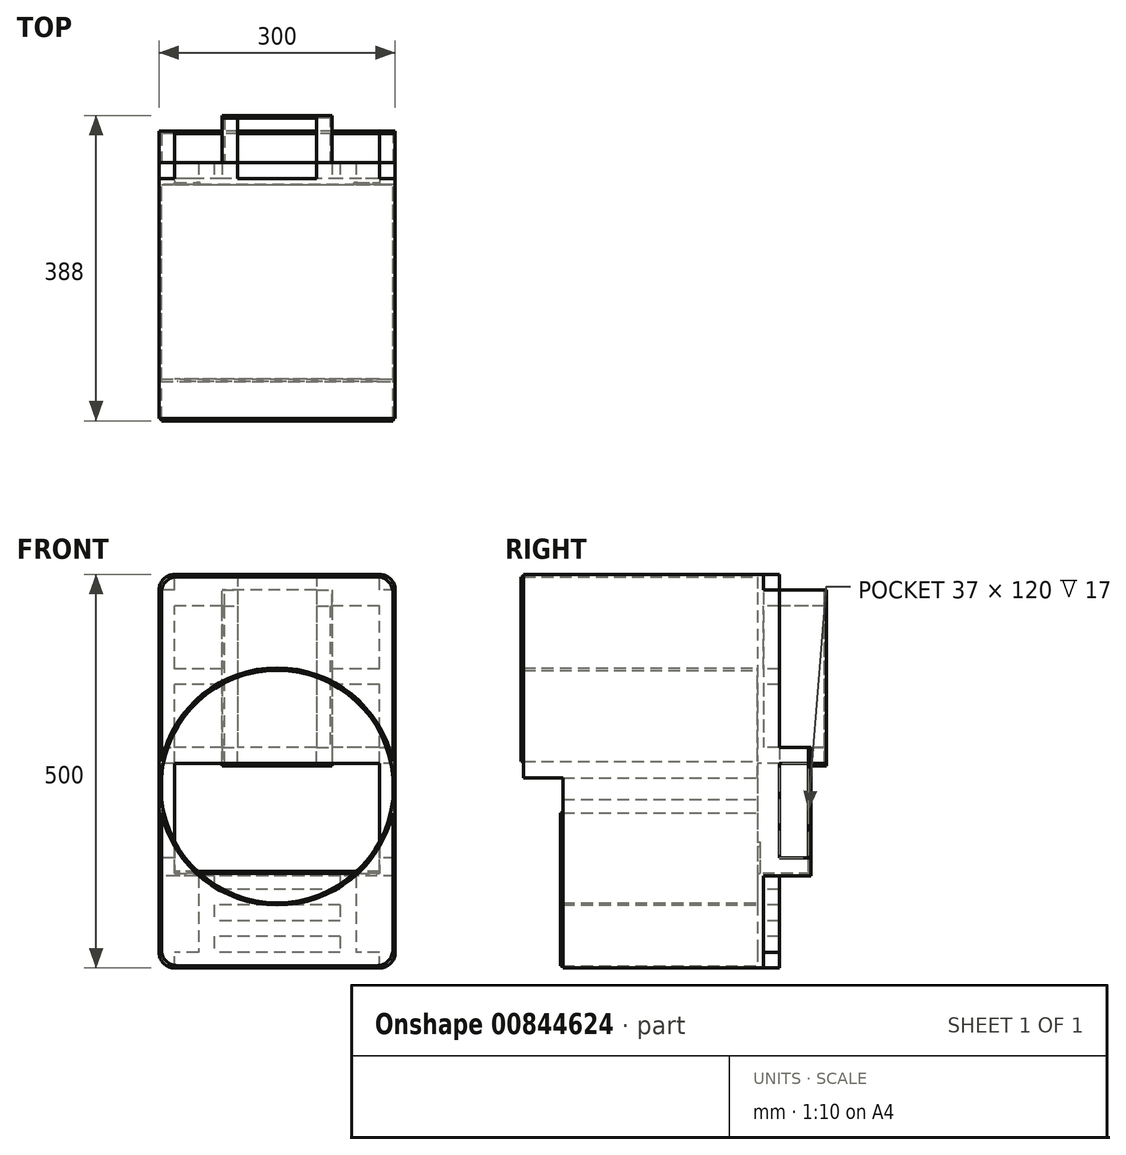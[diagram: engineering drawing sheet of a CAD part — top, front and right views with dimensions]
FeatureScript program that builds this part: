
annotation { "Feature Type Name" : "Feature", "Feature Type Description" : "" }
export const myFeature = defineFeature(function(context is Context, id is Id, definition is map)
    precondition{}
    {
        {
            var Q0;
            Q0=qCreatedBy(makeId("Front.planeOp"),FACE);
            var sketch = newSketch(context, id + "F0", { "sketchPlane" : qUnion([Q0])});
            skLineSegment(sketch, "E0.bottom", {"start": v(130, -250) * mm, "end": v(-130, -250) * mm});
            skLineSegment(sketch, "E0.top", {"start": v(130, 250) * mm, "end": v(-130, 250) * mm});
            skLineSegment(sketch, "E0.left", {"start": v(150, -230) * mm, "end": v(150, 230) * mm});
            skLineSegment(sketch, "E0.right", {"start": v(-150, -230) * mm, "end": v(-150, 230) * mm});
            skPoint(sketch, "E0.middle", {"position": v(0, 0) * mm});
            skPoint(sketch, "E1.visualSharp", {"position": v(-150, 250) * mm});
            skArc(sketch, "E1.filletArc", {"start": v(-130, 250) * mm, "mid": v(-144.14, 244.14) * mm, "end": v(-150, 230) * mm});
            skPoint(sketch, "E2.visualSharp", {"position": v(150, 250) * mm});
            skArc(sketch, "E2.filletArc", {"start": v(150, 230) * mm, "mid": v(144.14, 244.14) * mm, "end": v(130, 250) * mm});
            skPoint(sketch, "E3.visualSharp", {"position": v(-150, -250) * mm});
            skArc(sketch, "E3.filletArc", {"start": v(-150, -230) * mm, "mid": v(-144.14, -244.14) * mm, "end": v(-130, -250) * mm});
            skPoint(sketch, "E4.visualSharp", {"position": v(150, -250) * mm});
            skArc(sketch, "E4.filletArc", {"start": v(130, -250) * mm, "mid": v(144.14, -244.14) * mm, "end": v(150, -230) * mm});
            skSolve(sketch);
        }
        {
            var Q0;
            Q0=makeQuery(id+"F0.imprint","IMPRINT",FACE,{"disambiguationData":[TD([[makeQuery(id+"F0.imprint","IMPRINT",EDGE,{"derivedFrom":sQuery(id+"F0.wireOp",EDGE,"E0.bottom")}),-1.0]])]});
            extrude(context, id + "F1", {"entities" : qUnion([Q0]), "depth" : 5 * mm, "offsetDistance" : 25 * mm});
        }
        {
            var Q0;
            Q0=makeQuery(id+"F1.opExtrude","CAP_FACE",FACE,{"disambiguationData":[OSD([sQuery(id+"F0.wireOp",EDGE,"E0.bottom"),sQuery(id+"F0.wireOp",EDGE,"E0.top"),sQuery(id+"F0.wireOp",EDGE,"E0.left"),sQuery(id+"F0.wireOp",EDGE,"E0.right"),sQuery(id+"F0.wireOp",EDGE,"E1.filletArc"),sQuery(id+"F0.wireOp",EDGE,"E2.filletArc"),sQuery(id+"F0.wireOp",EDGE,"E3.filletArc"),sQuery(id+"F0.wireOp",EDGE,"E4.filletArc")])],"isStart":true});
            var sketch = newSketch(context, id + "F2", { "sketchPlane" : qUnion([Q0])});
            skLineSegment(sketch, "E5.0", {"start": v(-150, 230) * mm, "end": v(-50, 230) * mm});
            skLineSegment(sketch, "E6", {"start": v(-100, -130) * mm, "end": v(-100, -230) * mm});
            skLineSegment(sketch, "E7", {"start": v(100, -130) * mm, "end": v(100, -230) * mm});
            skLineSegment(sketch, "E8.trimOffspring", {"start": v(-130, -130) * mm, "end": v(-130, 250) * mm});
            skLineSegment(sketch, "E9.trimOffspring", {"start": v(130, -130) * mm, "end": v(130, 250) * mm});
            skLineSegment(sketch, "E10.bottom", {"start": v(-130, -250) * mm, "end": v(130, -250) * mm});
            skLineSegment(sketch, "E10.top", {"start": v(-130, -230) * mm, "end": v(130, -230) * mm});
            skLineSegment(sketch, "E10.left", {"start": v(-130, -250) * mm, "end": v(-130, -230) * mm});
            skLineSegment(sketch, "E10.right", {"start": v(130, -250) * mm, "end": v(130, -230) * mm});
            skLineSegment(sketch, "E11.0", {"start": v(-80, -210) * mm, "end": v(80, -210) * mm});
            skLineSegment(sketch, "E12.0", {"start": v(-80, -150) * mm, "end": v(80, -150) * mm});
            skLineSegment(sketch, "E13.0", {"start": v(-150, -130) * mm, "end": v(150, -130) * mm});
            skLineSegment(sketch, "E14.0", {"start": v(-150, -110) * mm, "end": v(150, -110) * mm});
            skLineSegment(sketch, "E15.0", {"start": v(-80, -130) * mm, "end": v(-80, -230) * mm});
            skLineSegment(sketch, "E16.0", {"start": v(80, -130) * mm, "end": v(80, -230) * mm});
            skLineSegment(sketch, "E17.trimOffspring", {"start": v(-80, -190) * mm, "end": v(80, -190) * mm});
            skLineSegment(sketch, "E18.trimOffspring", {"start": v(-80, -170) * mm, "end": v(80, -170) * mm});
            skLineSegment(sketch, "E19.0", {"start": v(-130, 130) * mm, "end": v(-70, 130) * mm});
            skLineSegment(sketch, "E20.0", {"start": v(-130, 110) * mm, "end": v(-70, 110) * mm});
            skLineSegment(sketch, "E21", {"start": v(-150, 30) * mm, "end": v(150, 30) * mm});
            skLineSegment(sketch, "E22.0", {"start": v(-150, 10) * mm, "end": v(150, 10) * mm});
            skLineSegment(sketch, "E23", {"start": v(-70, 230) * mm, "end": v(-70, 10) * mm});
            skLineSegment(sketch, "E24", {"start": v(70, 230) * mm, "end": v(70, 10) * mm});
            skLineSegment(sketch, "E25.0", {"start": v(50, 250) * mm, "end": v(50, 10) * mm});
            skLineSegment(sketch, "E26.0", {"start": v(-50, 250) * mm, "end": v(-50, 10) * mm});
            skLineSegment(sketch, "E27.trimOffspring", {"start": v(50, 230) * mm, "end": v(150, 230) * mm});
            skLineSegment(sketch, "E28.trimOffspring", {"start": v(70, 130) * mm, "end": v(130, 130) * mm});
            skLineSegment(sketch, "E29.trimOffspring", {"start": v(70, 110) * mm, "end": v(130, 110) * mm});
            skLineSegment(sketch, "E30.0", {"start": v(-130, 210) * mm, "end": v(-50, 210) * mm});
            skLineSegment(sketch, "E31.0", {"start": v(50, 210) * mm, "end": v(130, 210) * mm});
            skPoint(sketch, "E32.orphan", {"position": v(130, 30) * mm});
            skSolve(sketch);
        }
        {
            var Q0;
            Q0=makeQuery(id+"F2.imprint","IMPRINT",FACE,{"disambiguationData":[TD([[makeQuery(id+"F2.imprint","IMPRINT",EDGE,{"derivedFrom":sQuery(id+"F2.wireOp",EDGE,"E10.bottom")}),1.0]])]});
            var Q1;
            {var subQ0=sQuery(id+"F2.wireOp",EDGE,"E11.0");Q1=makeQuery(id+"F2.imprint","IMPRINT",FACE,{"disambiguationData":[TD([[makeQuery(id+"F2.imprint","IMPRINT",EDGE,{"derivedFrom":subQ0}),1.0]])]});}
            var Q2;
            {var subQ0=sQuery(id+"F2.wireOp",EDGE,"E12.0");Q2=makeQuery(id+"F2.imprint","IMPRINT",FACE,{"disambiguationData":[TD([[makeQuery(id+"F2.imprint","IMPRINT",EDGE,{"derivedFrom":subQ0}),-1.0]])]});}
            var Q3;
            {var subQ0=sQuery(id+"F2.wireOp",EDGE,"E13.0");var subQ2=sQuery(id+"F2.wireOp",EDGE,"E8.trimOffspring");var subQ3=makeQuery(id+"F2.imprint","INTERSECT",VERTEX,{"derivedFrom":[subQ2,subQ0]});Q3=makeQuery(id+"F2.imprint","IMPRINT",FACE,{"disambiguationData":[TD([[makeQuery(id+"F2.imprint","IMPRINT",EDGE,{"disambiguationData":[TD([[subQ3,-1.0]])],"derivedFrom":subQ2}),-1.0]])]});}
            var Q4;
            {var subQ4=sQuery(id+"F2.wireOp",EDGE,"E6");Q4=makeQuery(id+"F2.imprint","IMPRINT",FACE,{"disambiguationData":[TD([[makeQuery(id+"F2.imprint","IMPRINT",EDGE,{"derivedFrom":subQ4}),1.0]])]});}
            var Q5;
            {var subQ4=sQuery(id+"F2.wireOp",EDGE,"E7");Q5=makeQuery(id+"F2.imprint","IMPRINT",FACE,{"disambiguationData":[TD([[makeQuery(id+"F2.imprint","IMPRINT",EDGE,{"derivedFrom":subQ4}),-1.0]])]});}
            var Q6;
            {var subQ0=sQuery(id+"F2.wireOp",EDGE,"E13.0");var subQ1=sQuery(id+"F2.wireOp",EDGE,"E8.trimOffspring");var subQ2=makeQuery(id+"F2.imprint","INTERSECT",VERTEX,{"derivedFrom":[subQ1,subQ0]});Q6=makeQuery(id+"F2.imprint","IMPRINT",FACE,{"disambiguationData":[TD([[makeQuery(id+"F2.imprint","IMPRINT",EDGE,{"disambiguationData":[TD([[subQ2,-1.0]])],"derivedFrom":subQ1}),1.0]])]});}
            var Q7;
            {var subQ0=sQuery(id+"F2.wireOp",EDGE,"E14.0");var subQ1=sQuery(id+"F2.wireOp",EDGE,"E8.trimOffspring");var subQ2=makeQuery(id+"F2.imprint","INTERSECT",VERTEX,{"derivedFrom":[subQ1,subQ0]});Q7=makeQuery(id+"F2.imprint","IMPRINT",FACE,{"disambiguationData":[TD([[makeQuery(id+"F2.imprint","IMPRINT",EDGE,{"disambiguationData":[TD([[subQ2,-1.0]])],"derivedFrom":subQ1}),1.0]])]});}
            var Q8;
            {var subQ0=sQuery(id+"F2.wireOp",EDGE,"E22.0");var subQ1=sQuery(id+"F2.wireOp",EDGE,"E8.trimOffspring");var subQ2=makeQuery(id+"F2.imprint","INTERSECT",VERTEX,{"derivedFrom":[subQ1,subQ0]});Q8=makeQuery(id+"F2.imprint","IMPRINT",FACE,{"disambiguationData":[TD([[makeQuery(id+"F2.imprint","IMPRINT",EDGE,{"disambiguationData":[TD([[subQ2,-1.0]])],"derivedFrom":subQ1}),1.0]])]});}
            var Q9;
            {var subQ0=sQuery(id+"F2.wireOp",EDGE,"E22.0");var subQ1=sQuery(id+"F2.wireOp",EDGE,"E8.trimOffspring");var subQ2=makeQuery(id+"F2.imprint","INTERSECT",VERTEX,{"derivedFrom":[subQ1,subQ0]});Q9=makeQuery(id+"F2.imprint","IMPRINT",FACE,{"disambiguationData":[TD([[makeQuery(id+"F2.imprint","IMPRINT",EDGE,{"disambiguationData":[TD([[subQ2,-1.0]])],"derivedFrom":subQ1}),-1.0]])]});}
            var Q10;
            {var subQ0=sQuery(id+"F2.wireOp",EDGE,"E23");var subQ1=sQuery(id+"F2.wireOp",EDGE,"E21");var subQ2=makeQuery(id+"F2.imprint","INTERSECT",VERTEX,{"derivedFrom":[subQ1,subQ0]});Q10=makeQuery(id+"F2.imprint","IMPRINT",FACE,{"disambiguationData":[TD([[makeQuery(id+"F2.imprint","IMPRINT",EDGE,{"disambiguationData":[TD([[subQ2,-1.0]])],"derivedFrom":subQ1}),-1.0]])]});}
            var Q11;
            {var subQ0=sQuery(id+"F2.wireOp",EDGE,"E26.0");var subQ1=sQuery(id+"F2.wireOp",EDGE,"E21");var subQ2=makeQuery(id+"F2.imprint","INTERSECT",VERTEX,{"derivedFrom":[subQ1,subQ0]});Q11=makeQuery(id+"F2.imprint","IMPRINT",FACE,{"disambiguationData":[TD([[makeQuery(id+"F2.imprint","IMPRINT",EDGE,{"disambiguationData":[TD([[subQ2,-1.0]])],"derivedFrom":subQ1}),-1.0]])]});}
            var Q12;
            {var subQ0=sQuery(id+"F2.wireOp",EDGE,"E25.0");var subQ1=sQuery(id+"F2.wireOp",EDGE,"E21");var subQ2=makeQuery(id+"F2.imprint","INTERSECT",VERTEX,{"derivedFrom":[subQ1,subQ0]});Q12=makeQuery(id+"F2.imprint","IMPRINT",FACE,{"disambiguationData":[TD([[makeQuery(id+"F2.imprint","IMPRINT",EDGE,{"disambiguationData":[TD([[subQ2,-1.0]])],"derivedFrom":subQ1}),-1.0]])]});}
            var Q13;
            {var subQ0=sQuery(id+"F2.wireOp",EDGE,"E22.0");var subQ1=sQuery(id+"F2.wireOp",EDGE,"E9.trimOffspring");var subQ2=makeQuery(id+"F2.imprint","INTERSECT",VERTEX,{"derivedFrom":[subQ1,subQ0]});Q13=makeQuery(id+"F2.imprint","IMPRINT",FACE,{"disambiguationData":[TD([[makeQuery(id+"F2.imprint","IMPRINT",EDGE,{"disambiguationData":[TD([[subQ2,-1.0]])],"derivedFrom":subQ1}),1.0]])]});}
            var Q14;
            {var subQ0=sQuery(id+"F2.wireOp",EDGE,"E22.0");var subQ1=sQuery(id+"F2.wireOp",EDGE,"E9.trimOffspring");var subQ2=makeQuery(id+"F2.imprint","INTERSECT",VERTEX,{"derivedFrom":[subQ1,subQ0]});Q14=makeQuery(id+"F2.imprint","IMPRINT",FACE,{"disambiguationData":[TD([[makeQuery(id+"F2.imprint","IMPRINT",EDGE,{"disambiguationData":[TD([[subQ2,-1.0]])],"derivedFrom":subQ1}),-1.0]])]});}
            var Q15;
            {var subQ0=sQuery(id+"F2.wireOp",EDGE,"E14.0");var subQ1=sQuery(id+"F2.wireOp",EDGE,"E9.trimOffspring");var subQ2=makeQuery(id+"F2.imprint","INTERSECT",VERTEX,{"derivedFrom":[subQ1,subQ0]});Q15=makeQuery(id+"F2.imprint","IMPRINT",FACE,{"disambiguationData":[TD([[makeQuery(id+"F2.imprint","IMPRINT",EDGE,{"disambiguationData":[TD([[subQ2,-1.0]])],"derivedFrom":subQ1}),-1.0]])]});}
            var Q16;
            {var subQ0=sQuery(id+"F2.wireOp",EDGE,"E13.0");var subQ1=sQuery(id+"F2.wireOp",EDGE,"E9.trimOffspring");var subQ2=makeQuery(id+"F2.imprint","INTERSECT",VERTEX,{"derivedFrom":[subQ1,subQ0]});Q16=makeQuery(id+"F2.imprint","IMPRINT",FACE,{"disambiguationData":[TD([[makeQuery(id+"F2.imprint","IMPRINT",EDGE,{"disambiguationData":[TD([[subQ2,-1.0]])],"derivedFrom":subQ1}),-1.0]])]});}
            var Q17;
            {var subQ2=sQuery(id+"F2.wireOp",EDGE,"E21");var subQ7=sQuery(id+"F2.wireOp",EDGE,"E25.0");var subQ8=makeQuery(id+"F2.imprint","INTERSECT",VERTEX,{"derivedFrom":[subQ2,subQ7]});Q17=makeQuery(id+"F2.imprint","IMPRINT",FACE,{"disambiguationData":[TD([[makeQuery(id+"F2.imprint","IMPRINT",EDGE,{"disambiguationData":[TD([[subQ8,-1.0]])],"derivedFrom":subQ2}),1.0]])]});}
            var Q18;
            {var subQ0=sQuery(id+"F2.wireOp",EDGE,"E28.trimOffspring");Q18=makeQuery(id+"F2.imprint","IMPRINT",FACE,{"disambiguationData":[TD([[makeQuery(id+"F2.imprint","IMPRINT",EDGE,{"derivedFrom":subQ0}),-1.0]])]});}
            var Q19;
            {var subQ0=sQuery(id+"F2.wireOp",EDGE,"E9.trimOffspring");var subQ5=makeQuery(id+"F2.imprint","INTERSECT",VERTEX,{"derivedFrom":[subQ0,sQuery(id+"F2.wireOp",EDGE,"E29.trimOffspring")]});Q19=makeQuery(id+"F2.imprint","IMPRINT",FACE,{"disambiguationData":[TD([[makeQuery(id+"F2.imprint","IMPRINT",EDGE,{"disambiguationData":[TD([[subQ5,1.0]])],"derivedFrom":subQ0}),-1.0]])]});}
            var Q20;
            {var subQ0=sQuery(id+"F2.wireOp",EDGE,"E31.0");var subQ1=sQuery(id+"F2.wireOp",EDGE,"E9.trimOffspring");var subQ2=makeQuery(id+"F2.imprint","INTERSECT",VERTEX,{"derivedFrom":[subQ1,subQ0]});Q20=makeQuery(id+"F2.imprint","IMPRINT",FACE,{"disambiguationData":[TD([[makeQuery(id+"F2.imprint","IMPRINT",EDGE,{"disambiguationData":[TD([[subQ2,-1.0]])],"derivedFrom":subQ1}),1.0]])]});}
            var Q21;
            {var subQ0=sQuery(id+"F2.wireOp",EDGE,"E27.trimOffspring");var subQ1=sQuery(id+"F2.wireOp",EDGE,"E24");var subQ2=makeQuery(id+"F2.imprint","INTERSECT",VERTEX,{"derivedFrom":[subQ1,subQ0]});Q21=makeQuery(id+"F2.imprint","IMPRINT",FACE,{"disambiguationData":[TD([[makeQuery(id+"F2.imprint","IMPRINT",EDGE,{"disambiguationData":[TD([[subQ2,-1.0]])],"derivedFrom":subQ1}),-1.0]])]});}
            var Q22;
            {var subQ4=sQuery(id+"F2.wireOp",EDGE,"E25.0");var subQ6=makeQuery(id+"F1.opExtrude","CAP_EDGE",EDGE,{"disambiguationData":[OSD([sQuery(id+"F0.wireOp",EDGE,"E0.top")])],"isStart":true});var subQ7=makeQuery(id+"F2.imprint","INTERSECT",VERTEX,{"derivedFrom":[subQ6,subQ4]});Q22=makeQuery(id+"F2.imprint","IMPRINT",FACE,{"disambiguationData":[TD([[makeQuery(id+"F2.imprint","IMPRINT",EDGE,{"disambiguationData":[TD([[subQ7,-1.0]])],"derivedFrom":subQ4}),1.0]])]});}
            var Q23;
            {var subQ1=sQuery(id+"F2.wireOp",EDGE,"E5.0");var subQ8=makeQuery(id+"F2.imprint","INTERSECT",VERTEX,{"derivedFrom":[subQ1,sQuery(id+"F2.wireOp",EDGE,"E23")]});Q23=makeQuery(id+"F2.imprint","IMPRINT",FACE,{"disambiguationData":[TD([[makeQuery(id+"F2.imprint","IMPRINT",EDGE,{"disambiguationData":[TD([[subQ8,1.0]])],"derivedFrom":subQ1}),1.0]])]});}
            var Q24;
            {var subQ0=sQuery(id+"F2.wireOp",EDGE,"E23");var subQ1=sQuery(id+"F2.wireOp",EDGE,"E5.0");var subQ2=makeQuery(id+"F2.imprint","INTERSECT",VERTEX,{"derivedFrom":[subQ1,subQ0]});Q24=makeQuery(id+"F2.imprint","IMPRINT",FACE,{"disambiguationData":[TD([[makeQuery(id+"F2.imprint","IMPRINT",EDGE,{"disambiguationData":[TD([[subQ2,1.0]])],"derivedFrom":subQ1}),-1.0]])]});}
            var Q25;
            {var subQ0=sQuery(id+"F2.wireOp",EDGE,"E23");var subQ7=sQuery(id+"F2.wireOp",EDGE,"E21");var subQ8=makeQuery(id+"F2.imprint","INTERSECT",VERTEX,{"derivedFrom":[subQ7,subQ0]});Q25=makeQuery(id+"F2.imprint","IMPRINT",FACE,{"disambiguationData":[TD([[makeQuery(id+"F2.imprint","IMPRINT",EDGE,{"disambiguationData":[TD([[subQ8,-1.0]])],"derivedFrom":subQ7}),1.0]])]});}
            var Q26;
            {var subQ0=sQuery(id+"F2.wireOp",EDGE,"E19.0");Q26=makeQuery(id+"F2.imprint","IMPRINT",FACE,{"disambiguationData":[TD([[makeQuery(id+"F2.imprint","IMPRINT",EDGE,{"derivedFrom":subQ0}),-1.0]])]});}
            var Q27;
            {var subQ0=sQuery(id+"F2.wireOp",EDGE,"E8.trimOffspring");var subQ2=makeQuery(id+"F2.imprint","INTERSECT",VERTEX,{"derivedFrom":[subQ0,sQuery(id+"F2.wireOp",EDGE,"E20.0")]});Q27=makeQuery(id+"F2.imprint","IMPRINT",FACE,{"disambiguationData":[TD([[makeQuery(id+"F2.imprint","IMPRINT",EDGE,{"disambiguationData":[TD([[subQ2,1.0]])],"derivedFrom":subQ0}),1.0]])]});}
            var Q28;
            {var subQ0=sQuery(id+"F2.wireOp",EDGE,"E26.0");var subQ1=sQuery(id+"F2.wireOp",EDGE,"E5.0");var subQ2=makeQuery(id+"F2.imprint","INTERSECT",VERTEX,{"derivedFrom":[subQ1,subQ0]});Q28=makeQuery(id+"F2.imprint","IMPRINT",FACE,{"disambiguationData":[TD([[makeQuery(id+"F2.imprint","IMPRINT",EDGE,{"disambiguationData":[TD([[subQ2,1.0]])],"derivedFrom":subQ1}),-1.0]])]});}
            extrude(context, id + "F3", {"entities" : qUnion([Q0, Q1, Q2, Q3, Q4, Q5, Q6, Q7, Q8, Q9, Q10, Q11, Q12, Q13, Q14, Q15, Q16, Q17, Q18, Q19, Q20, Q21, Q22, Q23, Q24, Q25, Q26, Q27, Q28]), "operationType" : NewBodyOperationType.ADD, "depth" : 20 * mm, "offsetDistance" : 25 * mm});
        }
        {
            var Q0;
            {var subQ0=sQuery(id+"F2.wireOp",EDGE,"E13.0");var subQ1=sQuery(id+"F2.wireOp",EDGE,"E8.trimOffspring");var subQ2=makeQuery(id+"F2.imprint","INTERSECT",VERTEX,{"derivedFrom":[subQ1,subQ0]});Q0=makeQuery(id+"F2.imprint","IMPRINT",FACE,{"disambiguationData":[TD([[makeQuery(id+"F2.imprint","IMPRINT",EDGE,{"disambiguationData":[TD([[subQ2,-1.0]])],"derivedFrom":subQ1}),1.0]])]});}
            var Q1;
            {var subQ0=sQuery(id+"F2.wireOp",EDGE,"E22.0");var subQ1=sQuery(id+"F2.wireOp",EDGE,"E8.trimOffspring");var subQ2=makeQuery(id+"F2.imprint","INTERSECT",VERTEX,{"derivedFrom":[subQ1,subQ0]});Q1=makeQuery(id+"F2.imprint","IMPRINT",FACE,{"disambiguationData":[TD([[makeQuery(id+"F2.imprint","IMPRINT",EDGE,{"disambiguationData":[TD([[subQ2,-1.0]])],"derivedFrom":subQ1}),1.0]])]});}
            var Q2;
            {var subQ0=sQuery(id+"F2.wireOp",EDGE,"E13.0");var subQ1=sQuery(id+"F2.wireOp",EDGE,"E9.trimOffspring");var subQ2=makeQuery(id+"F2.imprint","INTERSECT",VERTEX,{"derivedFrom":[subQ1,subQ0]});Q2=makeQuery(id+"F2.imprint","IMPRINT",FACE,{"disambiguationData":[TD([[makeQuery(id+"F2.imprint","IMPRINT",EDGE,{"disambiguationData":[TD([[subQ2,-1.0]])],"derivedFrom":subQ1}),-1.0]])]});}
            var Q3;
            {var subQ0=sQuery(id+"F2.wireOp",EDGE,"E22.0");var subQ1=sQuery(id+"F2.wireOp",EDGE,"E9.trimOffspring");var subQ2=makeQuery(id+"F2.imprint","INTERSECT",VERTEX,{"derivedFrom":[subQ1,subQ0]});Q3=makeQuery(id+"F2.imprint","IMPRINT",FACE,{"disambiguationData":[TD([[makeQuery(id+"F2.imprint","IMPRINT",EDGE,{"disambiguationData":[TD([[subQ2,-1.0]])],"derivedFrom":subQ1}),-1.0]])]});}
            extrude(context, id + "F4", {"entities" : qUnion([Q0, Q1, Q2, Q3]), "operationType" : NewBodyOperationType.ADD, "depth" : 60 * mm, "offsetDistance" : 25 * mm});
        }
        {
            var Q0;
            {var subQ0=sQuery(id+"F2.wireOp",EDGE,"E25.0");var subQ1=sQuery(id+"F2.wireOp",EDGE,"E21");var subQ2=makeQuery(id+"F2.imprint","INTERSECT",VERTEX,{"derivedFrom":[subQ1,subQ0]});Q0=makeQuery(id+"F2.imprint","IMPRINT",FACE,{"disambiguationData":[TD([[makeQuery(id+"F2.imprint","IMPRINT",EDGE,{"disambiguationData":[TD([[subQ2,-1.0]])],"derivedFrom":subQ1}),-1.0]])]});}
            var Q1;
            {var subQ0=sQuery(id+"F2.wireOp",EDGE,"E26.0");var subQ1=sQuery(id+"F2.wireOp",EDGE,"E5.0");var subQ2=makeQuery(id+"F2.imprint","INTERSECT",VERTEX,{"derivedFrom":[subQ1,subQ0]});Q1=makeQuery(id+"F2.imprint","IMPRINT",FACE,{"disambiguationData":[TD([[makeQuery(id+"F2.imprint","IMPRINT",EDGE,{"disambiguationData":[TD([[subQ2,1.0]])],"derivedFrom":subQ1}),-1.0]])]});}
            var Q2;
            {var subQ0=sQuery(id+"F2.wireOp",EDGE,"E27.trimOffspring");var subQ1=sQuery(id+"F2.wireOp",EDGE,"E24");var subQ2=makeQuery(id+"F2.imprint","INTERSECT",VERTEX,{"derivedFrom":[subQ1,subQ0]});Q2=makeQuery(id+"F2.imprint","IMPRINT",FACE,{"disambiguationData":[TD([[makeQuery(id+"F2.imprint","IMPRINT",EDGE,{"disambiguationData":[TD([[subQ2,-1.0]])],"derivedFrom":subQ1}),-1.0]])]});}
            var Q3;
            {var subQ0=sQuery(id+"F2.wireOp",EDGE,"E23");var subQ1=sQuery(id+"F2.wireOp",EDGE,"E21");var subQ2=makeQuery(id+"F2.imprint","INTERSECT",VERTEX,{"derivedFrom":[subQ1,subQ0]});Q3=makeQuery(id+"F2.imprint","IMPRINT",FACE,{"disambiguationData":[TD([[makeQuery(id+"F2.imprint","IMPRINT",EDGE,{"disambiguationData":[TD([[subQ2,-1.0]])],"derivedFrom":subQ1}),-1.0]])]});}
            extrude(context, id + "F5", {"entities" : qUnion([Q0, Q1, Q2, Q3]), "operationType" : NewBodyOperationType.ADD, "depth" : 80 * mm, "offsetDistance" : 25 * mm});
        }
        {
            var Q0;
            Q0=makeQuery(id+"F4.opExtrude","CAP_FACE",FACE,{"disambiguationData":[OSD([sQuery(id+"F0.wireOp",EDGE,"E0.left"),sQuery(id+"F2.wireOp",EDGE,"E8.trimOffspring"),sQuery(id+"F2.wireOp",EDGE,"E21"),sQuery(id+"F2.wireOp",EDGE,"E22.0")])],"isStart":false});
            var sketch = newSketch(context, id + "F6", { "sketchPlane" : qUnion([Q0])});
            skLineSegment(sketch, "E33", {"start": v(-70, 30) * mm, "end": v(-150, 30) * mm});
            skLineSegment(sketch, "E34", {"start": v(-150, 30) * mm, "end": v(-150, -130) * mm});
            skLineSegment(sketch, "E35", {"start": v(-150, -130) * mm, "end": v(150, -130) * mm});
            skLineSegment(sketch, "E36", {"start": v(150, -130) * mm, "end": v(150, 30) * mm});
            skLineSegment(sketch, "E37", {"start": v(150, 30) * mm, "end": v(70, 30) * mm});
            skLineSegment(sketch, "E38", {"start": v(70, 30) * mm, "end": v(70, 10) * mm});
            skLineSegment(sketch, "E39", {"start": v(-70, 30) * mm, "end": v(-70, 10) * mm});
            skLineSegment(sketch, "E40", {"start": v(-70, 10) * mm, "end": v(70, 10) * mm});
            skSolve(sketch);
        }
        {
            var Q0;
            {var subQ0=sQuery(id+"F0.wireOp",EDGE,"E0.left");var subQ1=makeQuery(id+"F1.opExtrude","CAP_EDGE",EDGE,{"disambiguationData":[OSD([subQ0])],"isStart":true});Q0=makeQuery(id+"F4.boolean.opBoolean","MERGE",FACE,{"derivedFrom":[makeQuery(id+"F3.boolean.opBoolean","MERGE",FACE,{"derivedFrom":[makeQuery(id+"F1.opExtrude","SWEPT_FACE",FACE,{"disambiguationData":[OSD([subQ0])]}),makeQuery(id+"F3.opExtrude","SWEPT_FACE",FACE,{"disambiguationData":[OSD([subQ0])]})]}),makeQuery(id+"F4.opExtrude","SWEPT_FACE",FACE,{"disambiguationData":[OSD([subQ0]),TDD([makeQuery(id+"F2.imprint","IMPRINT",EDGE,{"disambiguationData":[TD([[makeQuery(id+"F2.imprint","INTERSECT",VERTEX,{"derivedFrom":[subQ1,sQuery(id+"F2.wireOp",EDGE,"E13.0")]}),-1.0]])],"derivedFrom":subQ1})])]}),makeQuery(id+"F4.opExtrude","SWEPT_FACE",FACE,{"disambiguationData":[OSD([subQ0]),TDD([makeQuery(id+"F2.imprint","IMPRINT",EDGE,{"disambiguationData":[TD([[makeQuery(id+"F2.imprint","INTERSECT",VERTEX,{"derivedFrom":[subQ1,sQuery(id+"F2.wireOp",EDGE,"E21")]}),1.0]])],"derivedFrom":subQ1})])]})]});}
            var sketch = newSketch(context, id + "F7", { "sketchPlane" : qUnion([Q0])});
            skLineSegment(sketch, "E41.bottom", {"start": v(60, 30) * mm, "end": v(-5, 30) * mm});
            skLineSegment(sketch, "E41.top", {"start": v(60, -130) * mm, "end": v(-5, -130) * mm});
            skLineSegment(sketch, "E41.left", {"start": v(60, 30) * mm, "end": v(60, -130) * mm});
            skLineSegment(sketch, "E41.right", {"start": v(-5, 30) * mm, "end": v(-5, -130) * mm});
            skSolve(sketch);
        }
        {
            var Q0;
            {var subQ1=sQuery(id+"F2.wireOp",EDGE,"E14.0");var subQ2=sQuery(id+"F0.wireOp",EDGE,"E0.left");var subQ3=makeQuery(id+"F4.opExtrude","SWEPT_EDGE",EDGE,{"disambiguationData":[OSD([subQ2,subQ1])]});Q0=makeQuery(id+"F7.imprint","IMPRINT",FACE,{"disambiguationData":[TD([[makeQuery(id+"F7.imprint","IMPRINT",EDGE,{"derivedFrom":subQ3}),-1.0]])]});}
            extrude(context, id + "F8", {"entities" : qUnion([Q0]), "oppositeDirection" : true, "depth" : 3 * mm, "offsetDistance" : 25 * mm});
        }
        {
            var Q0;
            {var subQ0=sQuery(id+"F2.wireOp",EDGE,"E13.0");var subQ1=makeQuery(id+"F2.imprint","INTERSECT",VERTEX,{"derivedFrom":[sQuery(id+"F2.wireOp",EDGE,"E8.trimOffspring"),subQ0]});var subQ2=makeQuery(id+"F2.imprint","IMPRINT",EDGE,{"disambiguationData":[TD([[subQ1,1.0]])],"derivedFrom":subQ0});Q0=makeQuery(id+"F4.boolean.opBoolean","MERGE",FACE,{"derivedFrom":[makeQuery(id+"F3.opExtrude","SWEPT_FACE",FACE,{"disambiguationData":[OSD([subQ0]),TDD([subQ2,makeQuery(id+"F2.imprint","IMPRINT",EDGE,{"disambiguationData":[TD([[makeQuery(id+"F2.imprint","INTERSECT",VERTEX,{"derivedFrom":[sQuery(id+"F2.wireOp",EDGE,"E6"),subQ0]}),1.0]])],"derivedFrom":subQ0})])]}),makeQuery(id+"F4.opExtrude","SWEPT_FACE",FACE,{"disambiguationData":[OSD([subQ0]),TDD([subQ2])]})]});}
            var sketch = newSketch(context, id + "F9", { "sketchPlane" : qUnion([Q0])});
            skPoint(sketch, "E42.oppositeSnap0", {"position": v(150, -30) * mm});
            skPoint(sketch, "E42.oppositeSnap1", {"position": v(115, -20) * mm});
            skLineSegment(sketch, "E42.top", {"start": v(-150, -20) * mm, "end": v(150, -20) * mm});
            skLineSegment(sketch, "E42.left", {"start": v(-150, -60) * mm, "end": v(-150, -20) * mm});
            skLineSegment(sketch, "E42.right", {"start": v(150, -60) * mm, "end": v(150, -20) * mm});
            skLineSegment(sketch, "E43", {"start": v(150, -60) * mm, "end": v(-150, -60) * mm});
            skSolve(sketch);
        }
        {
            var Q0;
            {var subQ0=sQuery(id+"F9.wireOp",EDGE,"E42.left");Q0=makeQuery(id+"F9.imprint","IMPRINT",FACE,{"disambiguationData":[TD([[makeQuery(id+"F9.imprint","IMPRINT",EDGE,{"derivedFrom":subQ0}),-1.0]])]});}
            extrude(context, id + "F10", {"entities" : qUnion([Q0]), "operationType" : NewBodyOperationType.ADD, "oppositeDirection" : true, "depth" : 3 * mm, "offsetDistance" : 25 * mm});
        }
        {
            var Q0;
            {var subQ0=sQuery(id+"F0.wireOp",EDGE,"E0.right");var subQ1=makeQuery(id+"F1.opExtrude","CAP_EDGE",EDGE,{"disambiguationData":[OSD([subQ0])],"isStart":true});Q0=makeQuery(id+"F4.boolean.opBoolean","MERGE",FACE,{"derivedFrom":[makeQuery(id+"F3.boolean.opBoolean","MERGE",FACE,{"derivedFrom":[makeQuery(id+"F1.opExtrude","SWEPT_FACE",FACE,{"disambiguationData":[OSD([subQ0])]}),makeQuery(id+"F3.opExtrude","SWEPT_FACE",FACE,{"disambiguationData":[OSD([subQ0])]})]}),makeQuery(id+"F4.opExtrude","SWEPT_FACE",FACE,{"disambiguationData":[OSD([subQ0]),TDD([makeQuery(id+"F2.imprint","IMPRINT",EDGE,{"disambiguationData":[TD([[makeQuery(id+"F2.imprint","INTERSECT",VERTEX,{"derivedFrom":[subQ1,sQuery(id+"F2.wireOp",EDGE,"E13.0")]}),-1.0]])],"derivedFrom":subQ1})])]}),makeQuery(id+"F4.opExtrude","SWEPT_FACE",FACE,{"disambiguationData":[OSD([subQ0]),TDD([makeQuery(id+"F2.imprint","IMPRINT",EDGE,{"disambiguationData":[TD([[makeQuery(id+"F2.imprint","INTERSECT",VERTEX,{"derivedFrom":[subQ1,sQuery(id+"F2.wireOp",EDGE,"E21")]}),1.0]])],"derivedFrom":subQ1})])]})]});}
            var sketch = newSketch(context, id + "F11", { "sketchPlane" : qUnion([Q0])});
            skLineSegment(sketch, "E44.bottom", {"start": v(-60, -130) * mm, "end": v(5, -130) * mm});
            skLineSegment(sketch, "E44.top", {"start": v(-60, 30) * mm, "end": v(5, 30) * mm});
            skLineSegment(sketch, "E44.left", {"start": v(-60, -130) * mm, "end": v(-60, 30) * mm});
            skLineSegment(sketch, "E44.right", {"start": v(5, -130) * mm, "end": v(5, 30) * mm});
            skSolve(sketch);
        }
        {
            var Q0;
            {var subQ1=sQuery(id+"F2.wireOp",EDGE,"E14.0");var subQ2=sQuery(id+"F0.wireOp",EDGE,"E0.right");var subQ3=makeQuery(id+"F4.opExtrude","SWEPT_EDGE",EDGE,{"disambiguationData":[OSD([subQ2,subQ1])]});Q0=makeQuery(id+"F11.imprint","IMPRINT",FACE,{"disambiguationData":[TD([[makeQuery(id+"F11.imprint","IMPRINT",EDGE,{"derivedFrom":subQ3}),1.0]])]});}
            extrude(context, id + "F12", {"entities" : qUnion([Q0]), "operationType" : NewBodyOperationType.ADD, "oppositeDirection" : true, "depth" : 3 * mm, "offsetDistance" : 25 * mm});
        }
        {
            var Q0;
            {var subQ0=sQuery(id+"F2.wireOp",EDGE,"E23");Q0=makeQuery(id+"F5.opExtrude","SWEPT_FACE",FACE,{"disambiguationData":[OSD([subQ0]),TDD([makeQuery(id+"F2.imprint","IMPRINT",EDGE,{"disambiguationData":[TD([[makeQuery(id+"F2.imprint","INTERSECT",VERTEX,{"derivedFrom":[sQuery(id+"F2.wireOp",EDGE,"E5.0"),subQ0]}),-1.0]])],"derivedFrom":subQ0})])]});}
            var sketch = newSketch(context, id + "F13", { "sketchPlane" : qUnion([Q0])});
            skLineSegment(sketch, "E45.bottom", {"start": v(80, 210) * mm, "end": v(20, 210) * mm});
            skLineSegment(sketch, "E45.top", {"start": v(80, 30) * mm, "end": v(20, 30) * mm});
            skLineSegment(sketch, "E45.left", {"start": v(80, 210) * mm, "end": v(80, 30) * mm});
            skLineSegment(sketch, "E45.right", {"start": v(20, 210) * mm, "end": v(20, 30) * mm});
            skSolve(sketch);
        }
        {
            var Q0;
            Q0=makeQuery(id+"F13.imprint","IMPRINT",FACE,{"disambiguationData":[TD([[makeQuery(id+"F13.imprint","IMPRINT",EDGE,{"derivedFrom":sQuery(id+"F13.wireOp",EDGE,"E45.bottom")}),1.0]])]});
            extrude(context, id + "F14", {"entities" : qUnion([Q0]), "operationType" : NewBodyOperationType.ADD, "oppositeDirection" : true, "depth" : 3 * mm, "offsetDistance" : 25 * mm});
        }
        {
            var Q0;
            {var subQ0=sQuery(id+"F2.wireOp",EDGE,"E14.0");var subQ1=sQuery(id+"F2.wireOp",EDGE,"E13.0");var subQ2=sQuery(id+"F2.wireOp",EDGE,"E9.trimOffspring");var subQ3=sQuery(id+"F0.wireOp",EDGE,"E0.right");Q0=makeQuery(id+"F12.boolean.opBoolean","MERGE",FACE,{"derivedFrom":[makeQuery(id+"F4.opExtrude","CAP_FACE",FACE,{"disambiguationData":[OSD([subQ3,subQ2,sQuery(id+"F2.wireOp",EDGE,"E21"),sQuery(id+"F2.wireOp",EDGE,"E22.0")])],"isStart":false}),makeQuery(id+"F10.boolean.opBoolean","MERGE",FACE,{"derivedFrom":[makeQuery(id+"F4.opExtrude","CAP_FACE",FACE,{"disambiguationData":[OSD([sQuery(id+"F0.wireOp",EDGE,"E0.left"),sQuery(id+"F2.wireOp",EDGE,"E8.trimOffspring"),subQ1,subQ0])],"isStart":false}),makeQuery(id+"F4.opExtrude","CAP_FACE",FACE,{"disambiguationData":[OSD([subQ3,subQ2,subQ1,subQ0])],"isStart":false}),makeQuery(id+"F10.opExtrude","SWEPT_FACE",FACE,{"disambiguationData":[OSD([sQuery(id+"F9.wireOp",EDGE,"E43")])]})]}),makeQuery(id+"F12.opExtrude","SWEPT_FACE",FACE,{"disambiguationData":[OSD([sQuery(id+"F11.wireOp",EDGE,"E44.left")])]})]});}
            var sketch = newSketch(context, id + "F15", { "sketchPlane" : qUnion([Q0])});
            skLineSegment(sketch, "E46.bottom", {"start": v(-150, 30) * mm, "end": v(-70, 30) * mm});
            skLineSegment(sketch, "E46.top", {"start": v(-150, -130) * mm, "end": v(150, -130) * mm});
            skLineSegment(sketch, "E46.left", {"start": v(-150, 30) * mm, "end": v(-150, -130) * mm});
            skLineSegment(sketch, "E46.right", {"start": v(150, 30) * mm, "end": v(150, -130) * mm});
            skLineSegment(sketch, "E47", {"start": v(-70, 30) * mm, "end": v(-70, 10) * mm});
            skLineSegment(sketch, "E48", {"start": v(-70, 10) * mm, "end": v(70, 10) * mm});
            skPoint(sketch, "E49", {"position": v(70, 10) * mm});
            skLineSegment(sketch, "E50", {"start": v(70, 30) * mm, "end": v(70, 10) * mm});
            skLineSegment(sketch, "E51.trimOffspring", {"start": v(70, 30) * mm, "end": v(150, 30) * mm});
            skSolve(sketch);
        }
        {
            var Q0;
            Q0 = qSketchRegion(id + "F15", true);
            extrude(context, id + "F16", {"entities" : qUnion([Q0]), "oppositeDirection" : true, "depth" : 3 * mm, "offsetDistance" : 25 * mm});
        }
        {
            var Q0;
            {var subQ11=sQuery(id+"F15.wireOp",EDGE,"E46.bottom");Q0=makeQuery(id+"F15.imprint","IMPRINT",FACE,{"disambiguationData":[TD([[makeQuery(id+"F15.imprint","IMPRINT",EDGE,{"derivedFrom":subQ11}),-1.0]])]});}
            extrude(context, id + "F17", {"entities" : qUnion([Q0]), "oppositeDirection" : true, "depth" : 3 * mm, "offsetDistance" : 25 * mm});
        }
        {
            var Q0;
            {var subQ0=sQuery(id+"F2.wireOp",EDGE,"E22.0");Q0=makeQuery(id+"F5.boolean.opBoolean","MERGE",FACE,{"derivedFrom":[makeQuery(id+"F3.opExtrude","SWEPT_FACE",FACE,{"disambiguationData":[OSD([subQ0])]}),makeQuery(id+"F5.opExtrude","SWEPT_FACE",FACE,{"disambiguationData":[OSD([subQ0]),TDD([makeQuery(id+"F2.imprint","IMPRINT",EDGE,{"disambiguationData":[TD([[makeQuery(id+"F2.imprint","INTERSECT",VERTEX,{"derivedFrom":[subQ0,sQuery(id+"F2.wireOp",EDGE,"E23")]}),-1.0]])],"derivedFrom":subQ0})])]}),makeQuery(id+"F5.opExtrude","SWEPT_FACE",FACE,{"disambiguationData":[OSD([subQ0]),TDD([makeQuery(id+"F2.imprint","IMPRINT",EDGE,{"disambiguationData":[TD([[makeQuery(id+"F2.imprint","INTERSECT",VERTEX,{"derivedFrom":[subQ0,sQuery(id+"F2.wireOp",EDGE,"E24")]}),1.0]])],"derivedFrom":subQ0})])]})]});}
            var sketch = newSketch(context, id + "F18", { "sketchPlane" : qUnion([Q0])});
            skLineSegment(sketch, "E52.bottom", {"start": v(70, -80) * mm, "end": v(-70, -80) * mm});
            skLineSegment(sketch, "E52.top", {"start": v(70, -57) * mm, "end": v(-70, -57) * mm});
            skLineSegment(sketch, "E52.left", {"start": v(70, -80) * mm, "end": v(70, -57) * mm});
            skLineSegment(sketch, "E52.right", {"start": v(-70, -80) * mm, "end": v(-70, -57) * mm});
            skSolve(sketch);
        }
        {
            var Q0;
            {var subQ0=sQuery(id+"F18.wireOp",EDGE,"E52.bottom");var subQ1=sQuery(id+"F2.wireOp",EDGE,"E22.0");var subQ2=makeQuery(id+"F5.opExtrude","SWEPT_EDGE",EDGE,{"disambiguationData":[OSD([subQ1,sQuery(id+"F2.wireOp",EDGE,"E25.0")])]});var subQ3=makeQuery(id+"F18.imprint","INTERSECT",VERTEX,{"derivedFrom":[subQ2,subQ0]});Q0=makeQuery(id+"F18.imprint","IMPRINT",FACE,{"disambiguationData":[TD([[makeQuery(id+"F18.imprint","IMPRINT",EDGE,{"disambiguationData":[TD([[subQ3,1.0]])],"derivedFrom":subQ0}),-1.0]])]});}
            var Q1;
            {var subQ0=sQuery(id+"F18.wireOp",EDGE,"E52.left");Q1=makeQuery(id+"F18.imprint","IMPRINT",FACE,{"disambiguationData":[TD([[makeQuery(id+"F18.imprint","IMPRINT",EDGE,{"derivedFrom":subQ0}),1.0]])]});}
            var Q2;
            {var subQ0=sQuery(id+"F18.wireOp",EDGE,"E52.right");Q2=makeQuery(id+"F18.imprint","IMPRINT",FACE,{"disambiguationData":[TD([[makeQuery(id+"F18.imprint","IMPRINT",EDGE,{"derivedFrom":subQ0}),-1.0]])]});}
            extrude(context, id + "F19", {"entities" : qUnion([Q0, Q1, Q2]), "depth" : 3 * mm, "offsetDistance" : 25 * mm});
        }
        {
            var Q0;
            {var subQ0=sQuery(id+"F2.wireOp",EDGE,"E26.0");var subQ1=sQuery(id+"F2.wireOp",EDGE,"E23");Q0=makeQuery(id+"F14.boolean.opBoolean","MERGE",FACE,{"derivedFrom":[makeQuery(id+"F5.opExtrude","CAP_FACE",FACE,{"disambiguationData":[OSD([sQuery(id+"F2.wireOp",EDGE,"E5.0"),subQ1,subQ0,sQuery(id+"F2.wireOp",EDGE,"E30.0")])],"isStart":false}),makeQuery(id+"F5.opExtrude","CAP_FACE",FACE,{"disambiguationData":[OSD([sQuery(id+"F2.wireOp",EDGE,"E21"),sQuery(id+"F2.wireOp",EDGE,"E22.0"),subQ1,subQ0])],"isStart":false}),makeQuery(id+"F14.opExtrude","SWEPT_FACE",FACE,{"disambiguationData":[OSD([sQuery(id+"F13.wireOp",EDGE,"E45.left")])]})]});}
            var sketch = newSketch(context, id + "F20", { "sketchPlane" : qUnion([Q0])});
            skLineSegment(sketch, "E53.bottom", {"start": v(-70, 7) * mm, "end": v(70, 7) * mm});
            skLineSegment(sketch, "E53.top", {"start": v(-70, 230) * mm, "end": v(70, 230) * mm});
            skLineSegment(sketch, "E53.left", {"start": v(-70, 7) * mm, "end": v(-70, 230) * mm});
            skLineSegment(sketch, "E53.right", {"start": v(70, 7) * mm, "end": v(70, 230) * mm});
            skSolve(sketch);
        }
        {
            var Q0;
            {var subQ6=sQuery(id+"F20.wireOp",EDGE,"E53.bottom");Q0=makeQuery(id+"F20.imprint","IMPRINT",FACE,{"disambiguationData":[TD([[makeQuery(id+"F20.imprint","IMPRINT",EDGE,{"derivedFrom":subQ6}),1.0]])]});}
            extrude(context, id + "F21", {"entities" : qUnion([Q0]), "oppositeDirection" : true, "depth" : 3 * mm, "offsetDistance" : 25 * mm});
        }
        {
            var Q0;
            Q0=makeQuery(id+"F1.opExtrude","CAP_FACE",FACE,{"disambiguationData":[OSD([sQuery(id+"F0.wireOp",EDGE,"E0.bottom"),sQuery(id+"F0.wireOp",EDGE,"E0.top"),sQuery(id+"F0.wireOp",EDGE,"E0.left"),sQuery(id+"F0.wireOp",EDGE,"E0.right"),sQuery(id+"F0.wireOp",EDGE,"E1.filletArc"),sQuery(id+"F0.wireOp",EDGE,"E2.filletArc"),sQuery(id+"F0.wireOp",EDGE,"E3.filletArc"),sQuery(id+"F0.wireOp",EDGE,"E4.filletArc")])],"isStart":false});
            var sketch = newSketch(context, id + "F22", { "sketchPlane" : qUnion([Q0])});
            skLineSegment(sketch, "E54.bottom", {"start": v(-150, 10) * mm, "end": v(150, 10) * mm});
            skLineSegment(sketch, "E54.top", {"start": v(-150, -130) * mm, "end": v(150, -130) * mm});
            skLineSegment(sketch, "E54.left", {"start": v(-150, 10) * mm, "end": v(-150, -130) * mm});
            skLineSegment(sketch, "E54.right", {"start": v(150, 10) * mm, "end": v(150, -130) * mm});
            skLineSegment(sketch, "E55.0", {"start": v(-130, 10) * mm, "end": v(-130, -130) * mm});
            skLineSegment(sketch, "E56.0", {"start": v(130, 10) * mm, "end": v(130, -130) * mm});
            skSolve(sketch);
        }
        {
            var Q0;
            {var subQ0=sQuery(id+"F22.wireOp",EDGE,"E55.0");Q0=makeQuery(id+"F22.imprint","IMPRINT",FACE,{"disambiguationData":[TD([[makeQuery(id+"F22.imprint","IMPRINT",EDGE,{"derivedFrom":subQ0}),1.0]])]});}
            extrude(context, id + "F23", {"entities" : qUnion([Q0]), "operationType" : NewBodyOperationType.REMOVE, "endBound" : BoundingType.UP_TO_NEXT, "oppositeDirection" : true, "depth" : 25 * mm, "offsetDistance" : 25 * mm});
        }
        {
            var Q0;
            {var subQ1=sQuery(id+"F0.wireOp",EDGE,"E0.left");var subQ4=sQuery(id+"F2.wireOp",EDGE,"E13.0");var subQ7=sQuery(id+"F2.wireOp",EDGE,"E8.trimOffspring");var subQ9=sQuery(id+"F2.wireOp",EDGE,"E9.trimOffspring");var subQ11=sQuery(id+"F9.wireOp",EDGE,"E43");var subQ12=makeQuery(id+"F2.imprint","INTERSECT",VERTEX,{"derivedFrom":[subQ7,subQ4]});var subQ13=makeQuery(id+"F2.imprint","INTERSECT",VERTEX,{"derivedFrom":[subQ9,subQ4]});var subQ14=makeQuery(id+"F2.imprint","IMPRINT",EDGE,{"disambiguationData":[TD([[subQ13,-1.0]])],"derivedFrom":subQ4});var subQ15=makeQuery(id+"F2.imprint","IMPRINT",EDGE,{"disambiguationData":[TD([[subQ12,1.0]])],"derivedFrom":subQ4});Q0=makeQuery(id+"F23.boolean.opBoolean","SPLIT",FACE,{"disambiguationData":[TD([makeQuery(id+"F1.opExtrude","SWEPT_FACE",FACE,{"disambiguationData":[OSD([subQ1])]})])],"derivedFrom":makeQuery(id+"F10.boolean.opBoolean","MERGE",FACE,{"derivedFrom":[makeQuery(id+"F3.opExtrude","SWEPT_FACE",FACE,{"disambiguationData":[OSD([subQ4]),TDD([makeQuery(id+"F2.imprint","IMPRINT",EDGE,{"disambiguationData":[TD([[makeQuery(id+"F2.imprint","INTERSECT",VERTEX,{"derivedFrom":[subQ4,sQuery(id+"F2.wireOp",EDGE,"E15.0")]}),-1.0]])],"derivedFrom":subQ4})])]}),makeQuery(id+"F4.boolean.opBoolean","MERGE",FACE,{"derivedFrom":[makeQuery(id+"F3.opExtrude","SWEPT_FACE",FACE,{"disambiguationData":[OSD([subQ4]),TDD([subQ15,makeQuery(id+"F2.imprint","IMPRINT",EDGE,{"disambiguationData":[TD([[makeQuery(id+"F2.imprint","INTERSECT",VERTEX,{"derivedFrom":[sQuery(id+"F2.wireOp",EDGE,"E6"),subQ4]}),1.0]])],"derivedFrom":subQ4})])]}),makeQuery(id+"F4.opExtrude","SWEPT_FACE",FACE,{"disambiguationData":[OSD([subQ4]),TDD([subQ15])]})]}),makeQuery(id+"F4.boolean.opBoolean","MERGE",FACE,{"derivedFrom":[makeQuery(id+"F3.opExtrude","SWEPT_FACE",FACE,{"disambiguationData":[OSD([subQ4]),TDD([makeQuery(id+"F2.imprint","IMPRINT",EDGE,{"disambiguationData":[TD([[makeQuery(id+"F2.imprint","INTERSECT",VERTEX,{"derivedFrom":[sQuery(id+"F2.wireOp",EDGE,"E7"),subQ4]}),-1.0]])],"derivedFrom":subQ4}),subQ14])]}),makeQuery(id+"F4.opExtrude","SWEPT_FACE",FACE,{"disambiguationData":[OSD([subQ4]),TDD([subQ14])]})]}),makeQuery(id+"F10.opExtrude","CAP_FACE",FACE,{"disambiguationData":[OSD([subQ7,subQ4,sQuery(id+"F9.wireOp",EDGE,"E42.top"),sQuery(id+"F9.wireOp",EDGE,"E42.left"),subQ11])],"isStart":true})]})});}
            var sketch = newSketch(context, id + "F24", { "sketchPlane" : qUnion([Q0])});
            skLineSegment(sketch, "E57.bottom", {"start": v(150, -60) * mm, "end": v(-150, -60) * mm});
            skLineSegment(sketch, "E57.top", {"start": v(150, 0) * mm, "end": v(-150, 0) * mm});
            skLineSegment(sketch, "E57.left", {"start": v(150, -60) * mm, "end": v(150, 0) * mm});
            skLineSegment(sketch, "E57.right", {"start": v(-150, -60) * mm, "end": v(-150, 0) * mm});
            skSolve(sketch);
        }
        {
            var Q0;
            {var subQ0=sQuery(id+"F24.wireOp",EDGE,"E57.left");Q0=makeQuery(id+"F24.imprint","IMPRINT",FACE,{"disambiguationData":[TD([[makeQuery(id+"F24.imprint","IMPRINT",EDGE,{"derivedFrom":subQ0}),1.0]])]});}
            var Q1;
            {var subQ10=sQuery(id+"F24.wireOp",EDGE,"E57.right");Q1=makeQuery(id+"F24.imprint","IMPRINT",FACE,{"disambiguationData":[TD([[makeQuery(id+"F24.imprint","IMPRINT",EDGE,{"derivedFrom":subQ10}),-1.0]])]});}
            extrude(context, id + "F25", {"entities" : qUnion([Q0, Q1]), "operationType" : NewBodyOperationType.ADD, "depth" : 3 * mm, "offsetDistance" : 25 * mm});
        }
        {
            var Q0;
            {var subQ0=sQuery(id+"F2.wireOp",EDGE,"E24");Q0=makeQuery(id+"F5.opExtrude","SWEPT_FACE",FACE,{"disambiguationData":[OSD([subQ0]),TDD([makeQuery(id+"F2.imprint","IMPRINT",EDGE,{"disambiguationData":[TD([[makeQuery(id+"F2.imprint","INTERSECT",VERTEX,{"derivedFrom":[subQ0,sQuery(id+"F2.wireOp",EDGE,"E27.trimOffspring")]}),-1.0]])],"derivedFrom":subQ0})])]});}
            var sketch = newSketch(context, id + "F26", { "sketchPlane" : qUnion([Q0])});
            skLineSegment(sketch, "E58.bottom", {"start": v(-77, 10) * mm, "end": v(-20, 10) * mm});
            skLineSegment(sketch, "E58.top", {"start": v(-77, 230) * mm, "end": v(-20, 230) * mm});
            skLineSegment(sketch, "E58.left", {"start": v(-77, 10) * mm, "end": v(-77, 230) * mm});
            skLineSegment(sketch, "E58.right", {"start": v(-20, 10) * mm, "end": v(-20, 230) * mm});
            skLineSegment(sketch, "E59", {"start": v(-77, 210) * mm, "end": v(-20, 210) * mm});
            skLineSegment(sketch, "E60", {"start": v(-77, 30) * mm, "end": v(-20, 30) * mm});
            skSolve(sketch);
        }
        {
            var Q0;
            {var subQ4=sQuery(id+"F26.wireOp",EDGE,"E58.bottom");Q0=makeQuery(id+"F26.imprint","IMPRINT",FACE,{"disambiguationData":[TD([[makeQuery(id+"F26.imprint","IMPRINT",EDGE,{"derivedFrom":subQ4}),1.0]])]});}
            extrude(context, id + "F27", {"entities" : qUnion([Q0]), "oppositeDirection" : true, "depth" : 3 * mm, "offsetDistance" : 25 * mm});
        }
        {
            var Q0;
            {var subQ5=sQuery(id+"F26.wireOp",EDGE,"E60");Q0=makeQuery(id+"F26.imprint","IMPRINT",FACE,{"disambiguationData":[TD([[makeQuery(id+"F26.imprint","IMPRINT",EDGE,{"derivedFrom":subQ5}),1.0]])]});}
            var Q1;
            {var subQ1=sQuery(id+"F2.wireOp",EDGE,"E24");var subQ2=makeQuery(id+"F5.opExtrude","CAP_EDGE",EDGE,{"disambiguationData":[OSD([subQ1]),TDD([makeQuery(id+"F2.imprint","IMPRINT",EDGE,{"disambiguationData":[TD([[makeQuery(id+"F2.imprint","INTERSECT",VERTEX,{"derivedFrom":[subQ1,sQuery(id+"F2.wireOp",EDGE,"E27.trimOffspring")]}),-1.0]])],"derivedFrom":subQ1})])],"isStart":false});Q1=makeQuery(id+"F26.imprint","IMPRINT",FACE,{"disambiguationData":[TD([[makeQuery(id+"F26.imprint","IMPRINT",EDGE,{"derivedFrom":subQ2}),1.0]])]});}
            var Q2;
            {var subQ0=sQuery(id+"F26.wireOp",EDGE,"E58.bottom");Q2=makeQuery(id+"F26.imprint","IMPRINT",FACE,{"disambiguationData":[TD([[makeQuery(id+"F26.imprint","IMPRINT",EDGE,{"derivedFrom":subQ0}),1.0]])]});}
            var Q3;
            {var subQ1=sQuery(id+"F2.wireOp",EDGE,"E24");var subQ2=makeQuery(id+"F5.opExtrude","CAP_EDGE",EDGE,{"disambiguationData":[OSD([subQ1]),TDD([makeQuery(id+"F2.imprint","IMPRINT",EDGE,{"disambiguationData":[TD([[makeQuery(id+"F2.imprint","INTERSECT",VERTEX,{"derivedFrom":[subQ1,sQuery(id+"F2.wireOp",EDGE,"E27.trimOffspring")]}),-1.0]])],"derivedFrom":subQ1})])],"isStart":false});Q3=makeQuery(id+"F26.imprint","IMPRINT",FACE,{"disambiguationData":[TD([[makeQuery(id+"F26.imprint","IMPRINT",EDGE,{"derivedFrom":subQ2}),-1.0]])]});}
            extrude(context, id + "F28", {"entities" : qUnion([Q0, Q1, Q2, Q3]), "oppositeDirection" : true, "depth" : 3 * mm, "offsetDistance" : 25 * mm});
        }
        {
            var Q0;
            Q0=makeQuery(id+"F1.opExtrude","CAP_FACE",FACE,{"disambiguationData":[OSD([sQuery(id+"F0.wireOp",EDGE,"E0.bottom"),sQuery(id+"F0.wireOp",EDGE,"E0.top"),sQuery(id+"F0.wireOp",EDGE,"E0.left"),sQuery(id+"F0.wireOp",EDGE,"E0.right"),sQuery(id+"F0.wireOp",EDGE,"E1.filletArc"),sQuery(id+"F0.wireOp",EDGE,"E2.filletArc"),sQuery(id+"F0.wireOp",EDGE,"E3.filletArc"),sQuery(id+"F0.wireOp",EDGE,"E4.filletArc")])],"isStart":false});
            var sketch = newSketch(context, id + "F29", { "sketchPlane" : qUnion([Q0])});
            skLineSegment(sketch, "E61.0", {"start": v(147, -227) * mm, "end": v(147, -53.28) * mm});
            skLineSegment(sketch, "E62.0", {"start": v(-147, -227) * mm, "end": v(-147, -53.28) * mm});
            skArc(sketch, "E63", {"start": v(-147, -35.57) * mm, "mid": v(0, -167.04) * mm, "end": v(147, -35.57) * mm});
            skArc(sketch, "E64.0", {"start": v(-147, -53.28) * mm, "mid": v(0, -170.04) * mm, "end": v(147, -53.28) * mm});
            skLineSegment(sketch, "E65.0", {"start": v(127, -247) * mm, "end": v(-127, -247) * mm});
            skPoint(sketch, "E66.visualSharp", {"position": v(-147, -247) * mm});
            skArc(sketch, "E66.filletArc", {"start": v(-147, -227) * mm, "mid": v(-141.14, -241.14) * mm, "end": v(-127, -247) * mm});
            skPoint(sketch, "E67.visualSharp", {"position": v(147, -247) * mm});
            skArc(sketch, "E67.filletArc", {"start": v(127, -247) * mm, "mid": v(141.14, -241.14) * mm, "end": v(147, -227) * mm});
            skLineSegment(sketch, "E68", {"start": v(-147, -35.57) * mm, "end": v(-150, -35.57) * mm});
            skLineSegment(sketch, "E69", {"start": v(147, -35.57) * mm, "end": v(150, -35.57) * mm});
            skLineSegment(sketch, "E70.0", {"start": v(-147, -230) * mm, "end": v(-147, -53.28) * mm});
            skLineSegment(sketch, "E71.0", {"start": v(147, -230) * mm, "end": v(147, -53.28) * mm});
            skLineSegment(sketch, "E72.0", {"start": v(127, 247) * mm, "end": v(-127, 247) * mm});
            skLineSegment(sketch, "E73.trimOffspring", {"start": v(-147, -35.57) * mm, "end": v(-147, -8.32) * mm});
            skLineSegment(sketch, "E74.trimOffspring", {"start": v(147, -35.57) * mm, "end": v(147, -8.32) * mm});
            skArc(sketch, "E75", {"start": v(147, -8.32) * mm, "mid": v(0, 128.28) * mm, "end": v(-147, -8.32) * mm});
            skLineSegment(sketch, "E76", {"start": v(147, -8.32) * mm, "end": v(150, -8.32) * mm});
            skPoint(sketch, "E77.visualSharp", {"position": v(147, 247) * mm});
            skArc(sketch, "E77.filletArc", {"start": v(147, 227) * mm, "mid": v(141.14, 241.14) * mm, "end": v(127, 247) * mm});
            skPoint(sketch, "E78.visualSharp", {"position": v(-147, 247) * mm});
            skArc(sketch, "E78.filletArc", {"start": v(-127, 247) * mm, "mid": v(-141.14, 241.14) * mm, "end": v(-147, 227) * mm});
            skLineSegment(sketch, "E79", {"start": v(-147, -8.32) * mm, "end": v(-150, -8.32) * mm});
            skArc(sketch, "E80.0", {"start": v(147, 12.66) * mm, "mid": v(0, 131.28) * mm, "end": v(-147, 12.66) * mm});
            skLineSegment(sketch, "E81.trimOffspring", {"start": v(-147, 12.66) * mm, "end": v(-147, 227) * mm});
            skLineSegment(sketch, "E82.trimOffspring", {"start": v(147, 12.66) * mm, "end": v(147, 227) * mm});
            skLineSegment(sketch, "E83", {"start": v(-147, -35.57) * mm, "end": v(-147, -53.28) * mm});
            skLineSegment(sketch, "E84", {"start": v(147, -35.57) * mm, "end": v(147, -53.28) * mm});
            skSolve(sketch);
        }
        {
            var Q0;
            {var subQ0=sQuery(id+"F29.wireOp",EDGE,"E67.filletArc");var subQ1=sQuery(id+"F29.wireOp",EDGE,"E66.filletArc");var subQ2=sQuery(id+"F29.wireOp",EDGE,"E65.0");var subQ3=sQuery(id+"F29.wireOp",EDGE,"E64.0");var subQ4=sQuery(id+"F29.wireOp",EDGE,"E62.0");var subQ5=sQuery(id+"F29.wireOp",EDGE,"E61.0");var subQ6=sQuery(id+"F0.wireOp",EDGE,"E4.filletArc");var subQ7=sQuery(id+"F0.wireOp",EDGE,"E3.filletArc");var subQ8=sQuery(id+"F0.wireOp",EDGE,"E0.right");var subQ9=sQuery(id+"F0.wireOp",EDGE,"E0.left");var subQ10=sQuery(id+"F0.wireOp",EDGE,"E0.bottom");var subQ11=sQuery(id+"F2.wireOp",EDGE,"E14.0");var subQ12=sQuery(id+"F2.wireOp",EDGE,"E8.trimOffspring");var subQ13=makeQuery(id+"F2.imprint","INTERSECT",VERTEX,{"derivedFrom":[subQ12,subQ11]});var subQ15=sQuery(id+"F2.wireOp",EDGE,"E13.0");var subQ16=sQuery(id+"F2.wireOp",EDGE,"E9.trimOffspring");var subQ17=makeQuery(id+"F2.imprint","INTERSECT",VERTEX,{"derivedFrom":[subQ16,subQ11]});Q0=makeQuery(id+"F4aI2tB48pUIwGg_9.boolean.opBoolean","SPLIT",FACE,{"disambiguationData":[TD([makeQuery(id+"F3.opExtrude","SWEPT_FACE",FACE,{"disambiguationData":[OSD([subQ12]),TDD([makeQuery(id+"F2.imprint","IMPRINT",EDGE,{"disambiguationData":[TD([[subQ13,-1.0]])],"derivedFrom":subQ12})])]}),makeQuery(id+"F3.opExtrude","SWEPT_FACE",FACE,{"disambiguationData":[OSD([subQ16]),TDD([makeQuery(id+"F2.imprint","IMPRINT",EDGE,{"disambiguationData":[TD([[subQ17,-1.0]])],"derivedFrom":subQ16})])]}),makeQuery(id+"F4.opExtrude","SWEPT_FACE",FACE,{"disambiguationData":[OSD([subQ12]),TDD([makeQuery(id+"F2.imprint","IMPRINT",EDGE,{"disambiguationData":[TD([[makeQuery(id+"F2.imprint","INTERSECT",VERTEX,{"derivedFrom":[subQ12,subQ15]}),-1.0]])],"derivedFrom":subQ12})])]}),makeQuery(id+"F4.opExtrude","SWEPT_FACE",FACE,{"disambiguationData":[OSD([subQ16]),TDD([makeQuery(id+"F2.imprint","IMPRINT",EDGE,{"disambiguationData":[TD([[makeQuery(id+"F2.imprint","INTERSECT",VERTEX,{"derivedFrom":[subQ16,subQ15]}),-1.0]])],"derivedFrom":subQ16})])]}),makeQuery(id+"F23.opExtrude","SWEPT_FACE",FACE,{"disambiguationData":[OSD([sQuery(id+"F22.wireOp",EDGE,"E55.0")])]}),makeQuery(id+"F23.opExtrude","SWEPT_FACE",FACE,{"disambiguationData":[OSD([sQuery(id+"F22.wireOp",EDGE,"E56.0")])]}),makeQuery(id+"F23.boolean.opBoolean","COPY",FACE,{"derivedFrom":makeQuery(id+"F23.opExtrude","SWEPT_FACE",FACE,{"disambiguationData":[OSD([sQuery(id+"F22.wireOp",EDGE,"E54.top")])]})}),makeQuery(id+"F25.opExtrude","CAP_FACE",FACE,{"disambiguationData":[OSD([sQuery(id+"F24.wireOp",EDGE,"E57.bottom"),sQuery(id+"F24.wireOp",EDGE,"E57.top"),sQuery(id+"F24.wireOp",EDGE,"E57.left"),sQuery(id+"F24.wireOp",EDGE,"E57.right")])],"isStart":true}),makeQuery(id+"F4aI2tB48pUIwGg_9.opExtrude","SWEPT_FACE",FACE,{"disambiguationData":[OSD([subQ5])]}),makeQuery(id+"F4aI2tB48pUIwGg_9.opExtrude","CAP_FACE",FACE,{"disambiguationData":[OSD([subQ10,subQ9,subQ8,subQ7,subQ6,subQ5,subQ4,sQuery(id+"F29.wireOp",EDGE,"E63"),subQ3,subQ2,subQ1,subQ0,sQuery(id+"F29.wireOp",EDGE,"E68"),sQuery(id+"F29.wireOp",EDGE,"E69")])],"isStart":true}),makeQuery(id+"F4aI2tB48pUIwGg_9.opExtrude","SWEPT_FACE",FACE,{"disambiguationData":[OSD([subQ4])]}),makeQuery(id+"F4aI2tB48pUIwGg_9.opExtrude","SWEPT_FACE",FACE,{"disambiguationData":[OSD([subQ3])]}),makeQuery(id+"F4aI2tB48pUIwGg_9.opExtrude","SWEPT_FACE",FACE,{"disambiguationData":[OSD([subQ2])]}),makeQuery(id+"F4aI2tB48pUIwGg_9.opExtrude","SWEPT_FACE",FACE,{"disambiguationData":[OSD([subQ1])]}),makeQuery(id+"F4aI2tB48pUIwGg_9.opExtrude","SWEPT_FACE",FACE,{"disambiguationData":[OSD([subQ0])]})])],"derivedFrom":makeQuery(id+"F1.opExtrude","CAP_FACE",FACE,{"disambiguationData":[OSD([subQ10,sQuery(id+"F0.wireOp",EDGE,"E0.top"),subQ9,subQ8,sQuery(id+"F0.wireOp",EDGE,"E1.filletArc"),sQuery(id+"F0.wireOp",EDGE,"E2.filletArc"),subQ7,subQ6])],"isStart":false})});}
            extrude(context, id + "F30", {"entities" : qUnion([Q0]), "operationType" : NewBodyOperationType.ADD, "depth" : 3 * mm, "offsetDistance" : 25 * mm});
        }
        {
            var Q0;
            Q0=makeQuery(id+"F29.imprint","IMPRINT",FACE,{"disambiguationData":[TD([[makeQuery(id+"F29.imprint","IMPRINT",EDGE,{"derivedFrom":sQuery(id+"F29.wireOp",EDGE,"E72.0")}),-1.0]])]});
            extrude(context, id + "F31", {"entities" : qUnion([Q0]), "operationType" : NewBodyOperationType.ADD, "depth" : 300 * mm, "offsetDistance" : 25 * mm});
        }
        {
            var Q0;
            {var subQ0=sQuery(id+"F29.wireOp",EDGE,"E69");Q0=makeQuery(id+"F29.imprint","IMPRINT",FACE,{"disambiguationData":[TD([[makeQuery(id+"F29.imprint","IMPRINT",EDGE,{"derivedFrom":subQ0}),1.0]])]});}
            var Q1;
            Q1=makeQuery(id+"F29.imprint","IMPRINT",FACE,{"disambiguationData":[TD([[makeQuery(id+"F29.imprint","IMPRINT",EDGE,{"derivedFrom":sQuery(id+"F29.wireOp",EDGE,"E65.0")}),1.0]])]});
            var Q2;
            {var subQ0=sQuery(id+"F29.wireOp",EDGE,"E84");Q2=makeQuery(id+"F29.imprint","IMPRINT",FACE,{"disambiguationData":[TD([[makeQuery(id+"F29.imprint","IMPRINT",EDGE,{"derivedFrom":subQ0}),-1.0]])]});}
            var Q3;
            {var subQ0=sQuery(id+"F29.wireOp",EDGE,"E68");Q3=makeQuery(id+"F29.imprint","IMPRINT",FACE,{"disambiguationData":[TD([[makeQuery(id+"F29.imprint","IMPRINT",EDGE,{"derivedFrom":subQ0}),-1.0]])]});}
            var Q4;
            {var subQ0=sQuery(id+"F29.wireOp",EDGE,"E83");Q4=makeQuery(id+"F29.imprint","IMPRINT",FACE,{"disambiguationData":[TD([[makeQuery(id+"F29.imprint","IMPRINT",EDGE,{"derivedFrom":subQ0}),1.0]])]});}
            var Q5;
            {var subQ0=sQuery(id+"F29.wireOp",EDGE,"E63");var subQ1=makeQuery(id+"F23.boolean.opBoolean","COPY",EDGE,{"derivedFrom":makeQuery(id+"F23.opExtrude","CAP_EDGE",EDGE,{"disambiguationData":[OSD([sQuery(id+"F22.wireOp",EDGE,"E55.0")])],"isStart":true})});var subQ2=makeQuery(id+"F29.imprint","INTERSECT",VERTEX,{"derivedFrom":[subQ1,subQ0]});Q5=makeQuery(id+"F29.imprint","IMPRINT",FACE,{"disambiguationData":[TD([[makeQuery(id+"F29.imprint","IMPRINT",EDGE,{"disambiguationData":[TD([[subQ2,-1.0]])],"derivedFrom":subQ0}),-1.0]])]});}
            var Q6;
            {var subQ0=sQuery(id+"F29.wireOp",EDGE,"E63");var subQ1=makeQuery(id+"F23.boolean.opBoolean","COPY",EDGE,{"derivedFrom":makeQuery(id+"F23.opExtrude","CAP_EDGE",EDGE,{"disambiguationData":[OSD([sQuery(id+"F22.wireOp",EDGE,"E54.top")])],"isStart":true})});var subQ2=makeQuery(id+"F29.imprint","INTERSECT",VERTEX,{"disambiguationData":[OD(0.0)],"derivedFrom":[subQ1,subQ0]});Q6=makeQuery(id+"F29.imprint","IMPRINT",FACE,{"disambiguationData":[TD([[makeQuery(id+"F29.imprint","IMPRINT",EDGE,{"disambiguationData":[TD([[subQ2,-1.0]])],"derivedFrom":subQ0}),-1.0]])]});}
            var Q7;
            {var subQ0=sQuery(id+"F29.wireOp",EDGE,"E63");var subQ1=makeQuery(id+"F23.boolean.opBoolean","COPY",EDGE,{"derivedFrom":makeQuery(id+"F23.opExtrude","CAP_EDGE",EDGE,{"disambiguationData":[OSD([sQuery(id+"F22.wireOp",EDGE,"E54.top")])],"isStart":true})});var subQ2=makeQuery(id+"F29.imprint","INTERSECT",VERTEX,{"disambiguationData":[OD(1.0)],"derivedFrom":[subQ1,subQ0]});Q7=makeQuery(id+"F29.imprint","IMPRINT",FACE,{"disambiguationData":[TD([[makeQuery(id+"F29.imprint","IMPRINT",EDGE,{"disambiguationData":[TD([[subQ2,-1.0]])],"derivedFrom":subQ0}),-1.0]])]});}
            extrude(context, id + "F32", {"entities" : qUnion([Q0, Q1, Q2, Q3, Q4, Q5, Q6, Q7]), "operationType" : NewBodyOperationType.ADD, "depth" : 250 * mm, "offsetDistance" : 25 * mm});
        }
        {
            var Q0;
            Q0=makeQuery(id+"F31.opExtrude","CAP_FACE",FACE,{"disambiguationData":[OSD([sQuery(id+"F0.wireOp",EDGE,"E0.top"),sQuery(id+"F0.wireOp",EDGE,"E0.left"),sQuery(id+"F0.wireOp",EDGE,"E0.right"),sQuery(id+"F0.wireOp",EDGE,"E1.filletArc"),sQuery(id+"F0.wireOp",EDGE,"E2.filletArc"),sQuery(id+"F29.wireOp",EDGE,"E72.0"),sQuery(id+"F29.wireOp",EDGE,"E75"),sQuery(id+"F29.wireOp",EDGE,"E76"),sQuery(id+"F29.wireOp",EDGE,"E77.filletArc"),sQuery(id+"F29.wireOp",EDGE,"E78.filletArc"),sQuery(id+"F29.wireOp",EDGE,"E79"),sQuery(id+"F29.wireOp",EDGE,"E80.0"),sQuery(id+"F29.wireOp",EDGE,"E81.trimOffspring"),sQuery(id+"F29.wireOp",EDGE,"E82.trimOffspring")])],"isStart":false});
            var sketch = newSketch(context, id + "F33", { "sketchPlane" : qUnion([Q0])});
            skSolve(sketch);
        }
        {
            var Q0;
            Q0=makeQuery(id+"F33.imprint","IMPRINT",FACE,{"disambiguationData":[TD([[makeQuery(id+"F33.imprint","IMPRINT",EDGE,{"derivedFrom":makeQuery(id+"F31.opExtrude","CAP_EDGE",EDGE,{"disambiguationData":[OSD([sQuery(id+"F29.wireOp",EDGE,"E72.0")])],"isStart":false})}),1.0]])]});
            extrude(context, id + "F34", {"entities" : qUnion([Q0]), "depth" : 3 * mm, "offsetDistance" : 25 * mm});
        }
        {
            var Q0;
            Q0=makeQuery(id+"F32.opExtrude","CAP_FACE",FACE,{"disambiguationData":[OSD([sQuery(id+"F0.wireOp",EDGE,"E0.bottom"),sQuery(id+"F0.wireOp",EDGE,"E0.left"),sQuery(id+"F0.wireOp",EDGE,"E0.right"),sQuery(id+"F0.wireOp",EDGE,"E3.filletArc"),sQuery(id+"F0.wireOp",EDGE,"E4.filletArc"),sQuery(id+"F29.wireOp",EDGE,"E63"),sQuery(id+"F29.wireOp",EDGE,"E64.0"),sQuery(id+"F29.wireOp",EDGE,"E65.0"),sQuery(id+"F29.wireOp",EDGE,"E66.filletArc"),sQuery(id+"F29.wireOp",EDGE,"E67.filletArc"),sQuery(id+"F29.wireOp",EDGE,"E70.0"),sQuery(id+"F29.wireOp",EDGE,"E71.0"),sQuery(id+"F29.wireOp",EDGE,"E73.trimOffspring"),sQuery(id+"F29.wireOp",EDGE,"E74.trimOffspring"),sQuery(id+"F29.wireOp",EDGE,"E76"),sQuery(id+"F29.wireOp",EDGE,"E79")])],"isStart":false});
            var sketch = newSketch(context, id + "F35", { "sketchPlane" : qUnion([Q0])});
            skSolve(sketch);
        }
        {
            var Q0;
            Q0=makeQuery(id+"F35.imprint","IMPRINT",FACE,{"disambiguationData":[TD([[makeQuery(id+"F35.imprint","IMPRINT",EDGE,{"derivedFrom":makeQuery(id+"F32.opExtrude","CAP_EDGE",EDGE,{"disambiguationData":[OSD([sQuery(id+"F29.wireOp",EDGE,"E64.0")])],"isStart":false})}),-1.0]])]});
            extrude(context, id + "F36", {"entities" : qUnion([Q0]), "depth" : 3 * mm, "offsetDistance" : 25 * mm});
        }
    });
